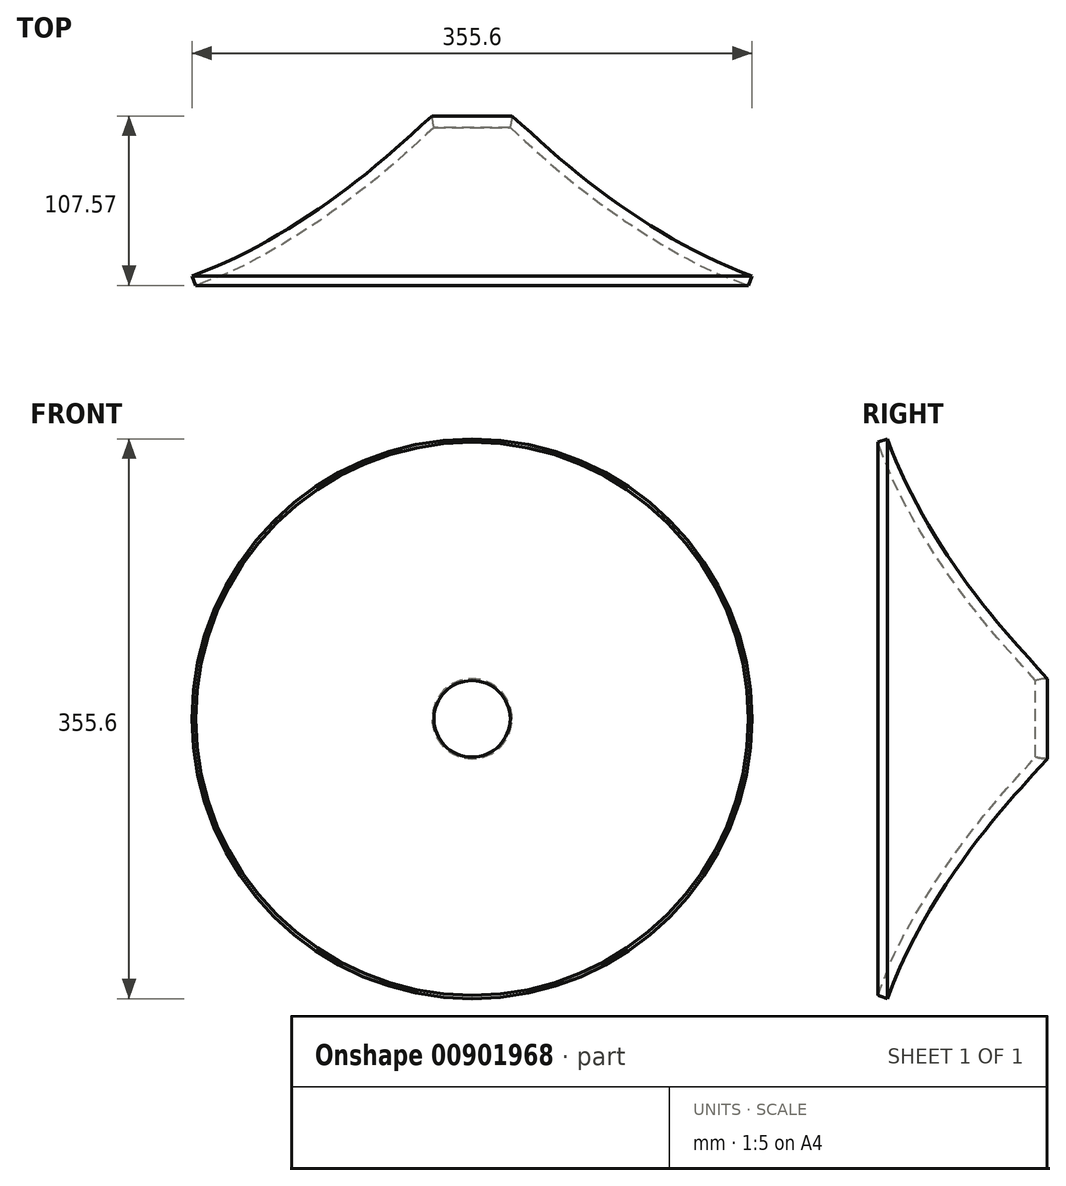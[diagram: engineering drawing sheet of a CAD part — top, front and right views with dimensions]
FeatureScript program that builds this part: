
annotation { "Feature Type Name" : "Feature", "Feature Type Description" : "" }
export const myFeature = defineFeature(function(context is Context, id is Id, definition is map)
    precondition{}
    {
        {
            var Q0;
            Q0=qCreatedBy(makeId("Right.planeOp"),FACE);
            var sketch = newSketch(context, id + "F0", { "sketchPlane" : qUnion([Q0])});
            skFitSpline(sketch, "E0", {"points": [v(-101.6, 177.8) * mm, v(-35.4, 65.7) * mm, v(0, 25.4) * mm], "startDerivative": vector(83.65, -231.4) * mm, "endDerivative": vector(114.11, -129.2) * mm});
            skArc(sketch, "E1", {"start": v(0, 25.4) * mm, "mid": v(-17.96, 17.96) * mm, "end": v(-25.4, 0) * mm});
            skArc(sketch, "E2.0", {"start": v(-12.05, 29.37) * mm, "mid": v(-26.37, 17.68) * mm, "end": v(-31.75, 0) * mm});
            skFitSpline(sketch, "E2.1", {"points": [v(-107.57, 175.64) * mm, v(-104, 165.77) * mm, v(-95.78, 146.57) * mm, v(-83.8, 124.41) * mm, v(-73.82, 108.06) * mm, v(-66.3, 96.56) * mm, v(-58.86, 85.9) * mm, v(-52.88, 77.77) * mm, v(-48.3, 71.75) * mm, v(-44.98, 67.5) * mm, v(-41.8, 63.5) * mm, v(-38.79, 59.8) * mm, v(-35.92, 56.33) * mm, v(-32.26, 51.99) * mm, v(-27.88, 46.95) * mm, v(-22.7, 41.15) * mm, v(-17.34, 35.23) * mm, v(-11.5, 28.78) * mm, v(-7.12, 23.87) * mm, v(-4.76, 21.2) * mm]});
            skLineSegment(sketch, "E3", {"start": v(-107.57, 175.64) * mm, "end": v(-101.6, 177.8) * mm});
            skLineSegment(sketch, "E4", {"start": v(-31.75, 0) * mm, "end": v(-25.4, 0) * mm});
            skSolve(sketch);
        }
        {
            var Q0;
            Q0=makeQuery(id+"F0.imprint","IMPRINT",FACE,{"disambiguationData":[TD([[makeQuery(id+"F0.imprint","IMPRINT",EDGE,{"derivedFrom":sQuery(id+"F0.wireOp",EDGE,"E0")}),-1.0]])]});
            var Q1;
            Q1=sQuery(id+"F0.wireOp",EDGE,"E4");
            revolve(context, id + "F1", {"surfaceOperationType" : NewSurfaceOperationType.NEW, "entities" : qUnion([Q0]), "axis" : qUnion([Q1]), "revolveType" : RevolveType.FULL});
        }
    });
